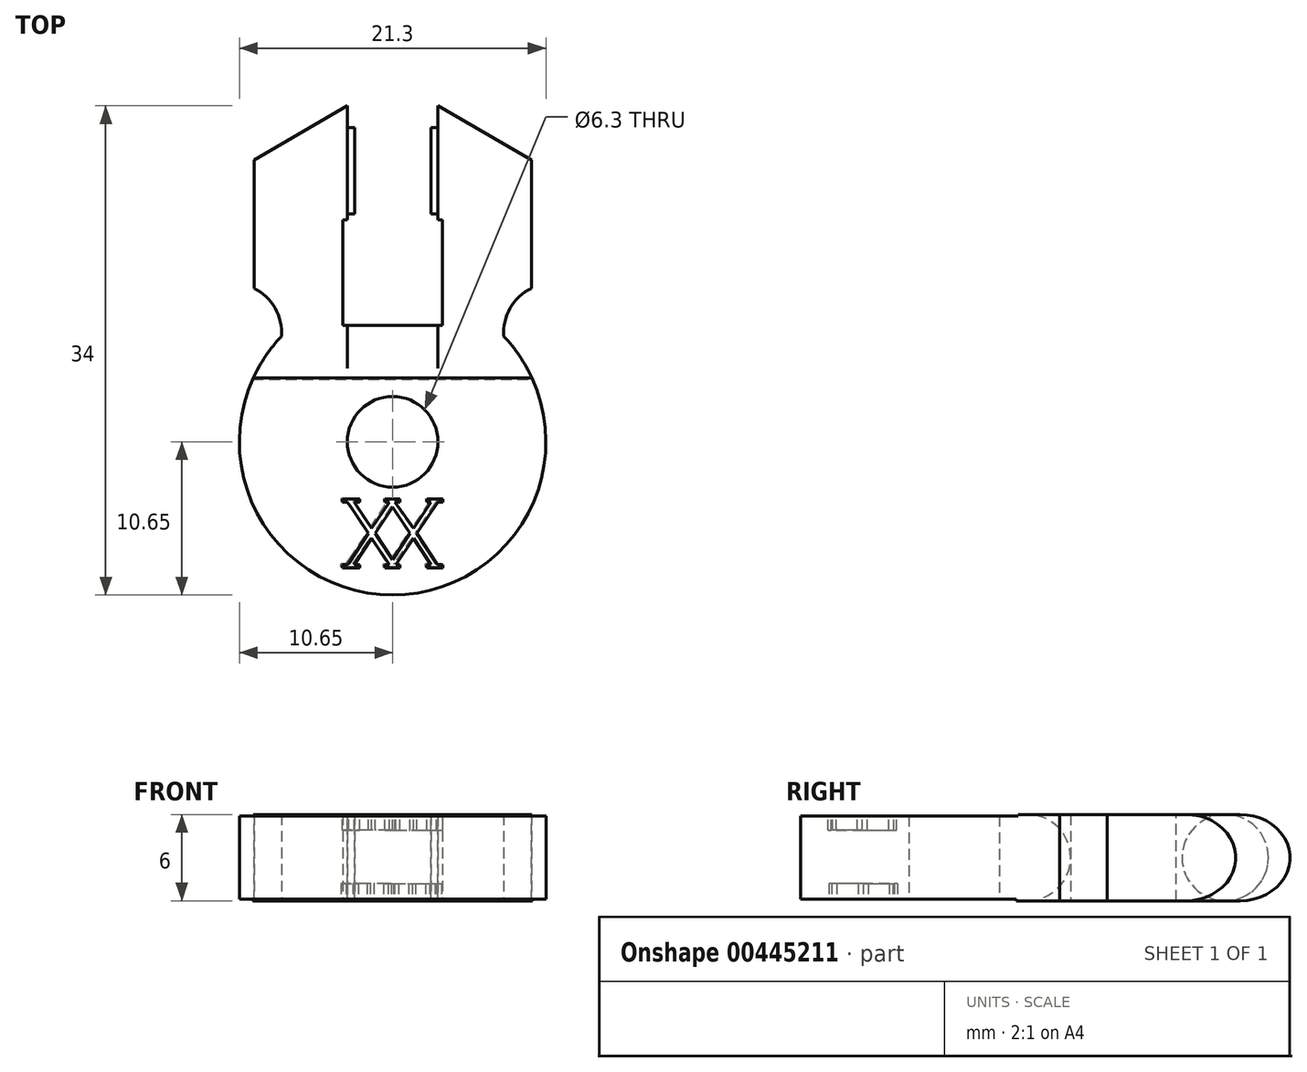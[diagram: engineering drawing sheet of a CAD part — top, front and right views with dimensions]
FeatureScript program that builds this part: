
annotation { "Feature Type Name" : "Feature", "Feature Type Description" : "" }
export const myFeature = defineFeature(function(context is Context, id is Id, definition is map)
    precondition{}
    {
        {
            var Q0;
            Q0=qCreatedBy(makeId("Top.planeOp"),FACE);
            var sketch = newSketch(context, id + "F0", { "sketchPlane" : qUnion([Q0])});
            skArc(sketch, "E0", {"start": v(-3.15, 10.17) * mm, "mid": v(0, -10.65) * mm, "end": v(3.15, 10.17) * mm});
            skCircle(sketch, "E1", {"center": v(0, 0) * mm, "radius": 3.15 * mm});
            skPoint(sketch, "E2", {"position": v(0, 8.1) * mm});
            skLineSegment(sketch, "E3", {"start": v(0, 8.1) * mm, "end": v(3.15, 8.1) * mm});
            skLineSegment(sketch, "E4", {"start": v(0, 8.1) * mm, "end": v(-3.15, 8.1) * mm});
            skLineSegment(sketch, "E5", {"start": v(0, 0) * mm, "end": v(0, 8.1) * mm});
            skLineSegment(sketch, "E6", {"start": v(-3.15, 8.1) * mm, "end": v(-3.15, 23.35) * mm});
            skLineSegment(sketch, "E7", {"start": v(-9.64, 19.59) * mm, "end": v(-9.64, 10.66) * mm});
            skLineSegment(sketch, "E8", {"start": v(-9.64, 19.59) * mm, "end": v(-3.15, 23.35) * mm});
            skArc(sketch, "E9", {"start": v(-7.72, 7.33) * mm, "mid": v(-8.17, 9.3) * mm, "end": v(-9.64, 10.66) * mm});
            skPoint(sketch, "E10.orphan", {"position": v(-9.64, 4.53) * mm});
            skLineSegment(sketch, "E11.MirrorCS", {"start": v(3.15, 8.1) * mm, "end": v(3.15, 23.35) * mm});
            skLineSegment(sketch, "E12.MirrorCS", {"start": v(9.64, 19.59) * mm, "end": v(3.15, 23.35) * mm});
            skLineSegment(sketch, "E13.MirrorCS", {"start": v(9.64, 19.59) * mm, "end": v(9.64, 10.66) * mm});
            skArc(sketch, "E14.MirrorCS", {"start": v(7.72, 7.33) * mm, "mid": v(8.17, 9.3) * mm, "end": v(9.64, 10.66) * mm});
            skSolve(sketch);
        }
        {
            var Q0;
            Q0 = qSketchRegion(id + "F0", true);
            extrude(context, id + "F1", {"entities" : qUnion([Q0]), "depth" : 6 * mm});
        }
        {
            var Q0;
            Q0=makeQuery(id+"F1.opExtrude","SWEPT_FACE",FACE,{"disambiguationData":[OSD([sQuery(id+"F0.wireOp",EDGE,"E6")])]});
            var sketch = newSketch(context, id + "F2", { "sketchPlane" : qUnion([Q0])});
            skLineSegment(sketch, "E15", {"start": v(23.35, 6) * mm, "end": v(23.35, 0) * mm});
            skPoint(sketch, "E16", {"position": v(23.35, 3) * mm});
            skCircle(sketch, "E17", {"center": v(18.85, 3) * mm, "radius": 3 * mm});
            skSolve(sketch);
        }
        {
            var Q0;
            Q0 = qSketchRegion(id + "F2", true);
            extrude(context, id + "F3", {"entities" : qUnion([Q0]), "operationType" : NewBodyOperationType.ADD, "depth" : 0.5 * mm});
        }
        {
            var Q0;
            Q0=makeQuery(id+"F1.opExtrude","SWEPT_FACE",FACE,{"disambiguationData":[OSD([sQuery(id+"F0.wireOp",EDGE,"E11.MirrorCS")])]});
            var sketch = newSketch(context, id + "F4", { "sketchPlane" : qUnion([Q0])});
            skPoint(sketch, "E18", {"position": v(-23.35, 3) * mm});
            skCircle(sketch, "E19", {"center": v(-18.85, 3) * mm, "radius": 3 * mm});
            skSolve(sketch);
        }
        {
            var Q0;
            Q0 = qSketchRegion(id + "F4", true);
            extrude(context, id + "F5", {"entities" : qUnion([Q0]), "operationType" : NewBodyOperationType.ADD, "depth" : 0.5 * mm});
        }
        {
            var Q0;
            Q0=makeQuery(id+"F1.opExtrude","CAP_EDGE",EDGE,{"disambiguationData":[OSD([sQuery(id+"F0.wireOp",EDGE,"E8")])],"isStart":true});
            var Q1;
            Q1=makeQuery(id+"F1.opExtrude","CAP_EDGE",EDGE,{"disambiguationData":[OSD([sQuery(id+"F0.wireOp",EDGE,"E8")])],"isStart":false});
            fillet(context, id + "F6", {"entities" : qUnion([Q0, Q1]), "radius" : 3 * mm, "tangentPropagation" : true, "allowEdgeOverflow" : false});
        }
        {
            var Q0;
            Q0=makeQuery(id+"F1.opExtrude","CAP_EDGE",EDGE,{"disambiguationData":[OSD([sQuery(id+"F0.wireOp",EDGE,"E12.MirrorCS")])],"isStart":true});
            var Q1;
            Q1=makeQuery(id+"F1.opExtrude","CAP_EDGE",EDGE,{"disambiguationData":[OSD([sQuery(id+"F0.wireOp",EDGE,"E12.MirrorCS")])],"isStart":false});
            fillet(context, id + "F7", {"entities" : qUnion([Q0, Q1]), "radius" : 3 * mm, "tangentPropagation" : true, "allowEdgeOverflow" : false});
        }
        {
            var Q0;
            Q0=makeQuery(id+"F1.opExtrude","CAP_FACE",FACE,{"disambiguationData":[OSD([sQuery(id+"F0.wireOp",EDGE,"E0"),sQuery(id+"F0.wireOp",EDGE,"E1"),sQuery(id+"F0.wireOp",EDGE,"E3"),sQuery(id+"F0.wireOp",EDGE,"E4"),sQuery(id+"F0.wireOp",EDGE,"E6"),sQuery(id+"F0.wireOp",EDGE,"E7"),sQuery(id+"F0.wireOp",EDGE,"E8"),sQuery(id+"F0.wireOp",EDGE,"E9"),sQuery(id+"F0.wireOp",EDGE,"E11.MirrorCS"),sQuery(id+"F0.wireOp",EDGE,"E12.MirrorCS"),sQuery(id+"F0.wireOp",EDGE,"E13.MirrorCS"),sQuery(id+"F0.wireOp",EDGE,"E14.MirrorCS")])],"isStart":false});
            var sketch = newSketch(context, id + "F8", { "sketchPlane" : qUnion([Q0])});
            skLineSegment(sketch, "E20.0", {"start": v(-0.23, -4.2) * mm, "end": v(-1.45, -6.02) * mm});
            skLineSegment(sketch, "E21.MirrorCS", {"start": v(0, -4.54) * mm, "end": v(-1.22, -6.37) * mm});
            skLineSegment(sketch, "E22.0", {"start": v(0, -8.2) * mm, "end": v(-1.22, -6.37) * mm});
            skLineSegment(sketch, "E23.MirrorCS", {"start": v(-0.23, -8.54) * mm, "end": v(-1.45, -6.72) * mm});
            skLineSegment(sketch, "E24.trimOffspring", {"start": v(-1.45, -6.02) * mm, "end": v(-2.67, -4.2) * mm});
            skLineSegment(sketch, "E25.trimOffspring", {"start": v(-1.45, -6.72) * mm, "end": v(-2.67, -8.54) * mm});
            skLineSegment(sketch, "E26.trimOffspring", {"start": v(-1.68, -6.37) * mm, "end": v(-2.9, -4.54) * mm});
            skLineSegment(sketch, "E27.trimOffspring", {"start": v(-1.68, -6.37) * mm, "end": v(-3.06, -8.44) * mm});
            skLineSegment(sketch, "E28.MirrorCS", {"start": v(0, -4.54) * mm, "end": v(1.22, -6.37) * mm});
            skLineSegment(sketch, "E29.MirrorCS", {"start": v(1.45, -6.02) * mm, "end": v(2.67, -4.2) * mm});
            skLineSegment(sketch, "E30.MirrorCS", {"start": v(1.68, -6.37) * mm, "end": v(2.9, -4.54) * mm});
            skLineSegment(sketch, "E31.MirrorCS", {"start": v(1.68, -6.37) * mm, "end": v(3.06, -8.44) * mm});
            skLineSegment(sketch, "E32.MirrorCS", {"start": v(1.45, -6.72) * mm, "end": v(2.67, -8.54) * mm});
            skLineSegment(sketch, "E33.MirrorCS", {"start": v(0.23, -8.54) * mm, "end": v(1.45, -6.72) * mm});
            skLineSegment(sketch, "E34.MirrorCS", {"start": v(0, -8.2) * mm, "end": v(1.22, -6.37) * mm});
            skLineSegment(sketch, "E35", {"start": v(0.16, -4.2) * mm, "end": v(0.5, -4.2) * mm});
            skLineSegment(sketch, "E36", {"start": v(-0.23, -4.2) * mm, "end": v(-0.54, -4.2) * mm});
            skLineSegment(sketch, "E37", {"start": v(-2.9, -4.54) * mm, "end": v(-3.13, -4.2) * mm});
            skLineSegment(sketch, "E38", {"start": v(2.9, -4.54) * mm, "end": v(3.13, -4.2) * mm});
            skLineSegment(sketch, "E39", {"start": v(3.06, -8.44) * mm, "end": v(3.14, -8.54) * mm});
            skLineSegment(sketch, "E40", {"start": v(-3.06, -8.44) * mm, "end": v(-3.14, -8.54) * mm});
            skLineSegment(sketch, "E41", {"start": v(-3.5, -4.2) * mm, "end": v(-3.13, -4.2) * mm});
            skLineSegment(sketch, "E42", {"start": v(-0.54, -4.2) * mm, "end": v(-0.23, -4.2) * mm});
            skLineSegment(sketch, "E43", {"start": v(2.38, -4.2) * mm, "end": v(2.67, -4.2) * mm});
            skLineSegment(sketch, "E44", {"start": v(-3.5, -4.2) * mm, "end": v(-3.5, -3.98) * mm});
            skLineSegment(sketch, "E45", {"start": v(-3.5, -3.98) * mm, "end": v(-2.3, -3.98) * mm});
            skLineSegment(sketch, "E46", {"start": v(3.5, -3.98) * mm, "end": v(3.5, -4.2) * mm});
            skLineSegment(sketch, "E47", {"start": v(-2.3, -4.2) * mm, "end": v(-2.3, -3.98) * mm});
            skLineSegment(sketch, "E48", {"start": v(-0.54, -4.2) * mm, "end": v(-0.54, -3.98) * mm});
            skLineSegment(sketch, "E49", {"start": v(0.5, -4.2) * mm, "end": v(0.5, -3.98) * mm});
            skLineSegment(sketch, "E50.trimOffspring", {"start": v(-0.54, -3.98) * mm, "end": v(0.5, -3.98) * mm});
            skLineSegment(sketch, "E51.trimOffspring", {"start": v(-2.3, -4.2) * mm, "end": v(-2.67, -4.2) * mm});
            skLineSegment(sketch, "E52.trimOffspring", {"start": v(-2.67, -4.2) * mm, "end": v(-2.3, -4.2) * mm});
            skLineSegment(sketch, "E53.trimOffspring", {"start": v(-3.13, -4.2) * mm, "end": v(-3.5, -4.2) * mm});
            skLineSegment(sketch, "E54", {"start": v(2.38, -4.2) * mm, "end": v(2.38, -3.98) * mm});
            skLineSegment(sketch, "E55.trimOffspring", {"start": v(2.38, -3.98) * mm, "end": v(3.5, -3.98) * mm});
            skLineSegment(sketch, "E56.trimOffspring", {"start": v(3.13, -4.2) * mm, "end": v(3.36, -4.2) * mm});
            skLineSegment(sketch, "E57.trimOffspring", {"start": v(3.13, -4.2) * mm, "end": v(3.5, -4.2) * mm});
            skLineSegment(sketch, "E58.trimOffspring", {"start": v(3.13, -8.54) * mm, "end": v(3.14, -8.54) * mm});
            skLineSegment(sketch, "E59.MirrorCS", {"start": v(-0.54, -8.75) * mm, "end": v(0.5, -8.75) * mm});
            skLineSegment(sketch, "E60.MirrorCS", {"start": v(-0.54, -8.54) * mm, "end": v(-0.54, -8.75) * mm});
            skLineSegment(sketch, "E61.MirrorCS", {"start": v(-0.23, -8.54) * mm, "end": v(-0.54, -8.54) * mm});
            skLineSegment(sketch, "E62.MirrorCS", {"start": v(0.23, -8.54) * mm, "end": v(0.5, -8.54) * mm});
            skLineSegment(sketch, "E63.MirrorCS", {"start": v(0.5, -8.54) * mm, "end": v(0.5, -8.75) * mm});
            skLineSegment(sketch, "E64.MirrorCS", {"start": v(-3.13, -8.54) * mm, "end": v(-3.5, -8.54) * mm});
            skLineSegment(sketch, "E65.MirrorCS", {"start": v(-3.5, -8.54) * mm, "end": v(-3.5, -8.75) * mm});
            skLineSegment(sketch, "E66.MirrorCS", {"start": v(-3.5, -8.75) * mm, "end": v(-2.3, -8.75) * mm});
            skLineSegment(sketch, "E67.MirrorCS", {"start": v(-2.3, -8.54) * mm, "end": v(-2.3, -8.75) * mm});
            skLineSegment(sketch, "E68.MirrorCS", {"start": v(-2.67, -8.54) * mm, "end": v(-2.3, -8.54) * mm});
            skLineSegment(sketch, "E69.MirrorCS", {"start": v(2.38, -8.75) * mm, "end": v(3.5, -8.75) * mm});
            skLineSegment(sketch, "E70.MirrorCS", {"start": v(3.5, -8.75) * mm, "end": v(3.5, -8.54) * mm});
            skLineSegment(sketch, "E71.MirrorCS", {"start": v(3.13, -8.54) * mm, "end": v(3.5, -8.54) * mm});
            skLineSegment(sketch, "E72.MirrorCS", {"start": v(2.38, -8.54) * mm, "end": v(2.67, -8.54) * mm});
            skLineSegment(sketch, "E73.MirrorCS", {"start": v(2.38, -8.54) * mm, "end": v(2.38, -8.75) * mm});
            skLineSegment(sketch, "E74", {"start": v(0.16, -4.2) * mm, "end": v(1.45, -6.02) * mm});
            skSolve(sketch);
        }
        {
            var Q0;
            Q0 = qSketchRegion(id + "F8", true);
            extrude(context, id + "F9", {"entities" : qUnion([Q0]), "operationType" : NewBodyOperationType.REMOVE, "oppositeDirection" : true, "depth" : 1.1 * mm});
        }
        {
            var Q0;
            Q0=makeQuery(id+"F1.opExtrude","CAP_FACE",FACE,{"disambiguationData":[OSD([sQuery(id+"F0.wireOp",EDGE,"E0"),sQuery(id+"F0.wireOp",EDGE,"E1"),sQuery(id+"F0.wireOp",EDGE,"E3"),sQuery(id+"F0.wireOp",EDGE,"E4"),sQuery(id+"F0.wireOp",EDGE,"E6"),sQuery(id+"F0.wireOp",EDGE,"E7"),sQuery(id+"F0.wireOp",EDGE,"E8"),sQuery(id+"F0.wireOp",EDGE,"E9"),sQuery(id+"F0.wireOp",EDGE,"E11.MirrorCS"),sQuery(id+"F0.wireOp",EDGE,"E12.MirrorCS"),sQuery(id+"F0.wireOp",EDGE,"E13.MirrorCS"),sQuery(id+"F0.wireOp",EDGE,"E14.MirrorCS")])],"isStart":true});
            var sketch = newSketch(context, id + "F10", { "sketchPlane" : qUnion([Q0])});
            skLineSegment(sketch, "E75.0", {"start": v(-0.33, 8.5) * mm, "end": v(-1.55, 6.67) * mm});
            skLineSegment(sketch, "E76.MirrorCS", {"start": v(-0.1, 8.14) * mm, "end": v(-1.32, 6.32) * mm});
            skLineSegment(sketch, "E77.0", {"start": v(-0.1, 4.5) * mm, "end": v(-1.32, 6.32) * mm});
            skLineSegment(sketch, "E78.MirrorCS", {"start": v(-0.33, 4.14) * mm, "end": v(-1.55, 5.97) * mm});
            skLineSegment(sketch, "E79.trimOffspring", {"start": v(-1.55, 6.67) * mm, "end": v(-2.77, 8.5) * mm});
            skLineSegment(sketch, "E80.trimOffspring", {"start": v(-1.55, 5.97) * mm, "end": v(-2.77, 4.14) * mm});
            skLineSegment(sketch, "E81.trimOffspring", {"start": v(-1.78, 6.32) * mm, "end": v(-3, 8.14) * mm});
            skLineSegment(sketch, "E82.trimOffspring", {"start": v(-1.78, 6.32) * mm, "end": v(-3.16, 4.25) * mm});
            skLineSegment(sketch, "E83.MirrorCS", {"start": v(-0.1, 8.14) * mm, "end": v(1.12, 6.32) * mm});
            skLineSegment(sketch, "E84.MirrorCS", {"start": v(1.35, 6.67) * mm, "end": v(2.57, 8.5) * mm});
            skLineSegment(sketch, "E85.MirrorCS", {"start": v(1.58, 6.32) * mm, "end": v(2.8, 8.14) * mm});
            skLineSegment(sketch, "E86.MirrorCS", {"start": v(1.58, 6.32) * mm, "end": v(2.96, 4.25) * mm});
            skLineSegment(sketch, "E87.MirrorCS", {"start": v(1.35, 5.97) * mm, "end": v(2.57, 4.14) * mm});
            skLineSegment(sketch, "E88.MirrorCS", {"start": v(0.13, 4.14) * mm, "end": v(1.35, 5.97) * mm});
            skLineSegment(sketch, "E89.MirrorCS", {"start": v(-0.1, 4.5) * mm, "end": v(1.12, 6.32) * mm});
            skLineSegment(sketch, "E90", {"start": v(0.06, 8.5) * mm, "end": v(0.4, 8.5) * mm});
            skLineSegment(sketch, "E91", {"start": v(-0.33, 8.5) * mm, "end": v(-0.64, 8.5) * mm});
            skLineSegment(sketch, "E92", {"start": v(-3, 8.14) * mm, "end": v(-3.23, 8.5) * mm});
            skLineSegment(sketch, "E93", {"start": v(2.8, 8.14) * mm, "end": v(3.03, 8.5) * mm});
            skLineSegment(sketch, "E94", {"start": v(2.96, 4.25) * mm, "end": v(3.04, 4.14) * mm});
            skLineSegment(sketch, "E95", {"start": v(-3.16, 4.25) * mm, "end": v(-3.24, 4.14) * mm});
            skLineSegment(sketch, "E96", {"start": v(-3.6, 8.5) * mm, "end": v(-3.23, 8.5) * mm});
            skLineSegment(sketch, "E97", {"start": v(-0.64, 8.5) * mm, "end": v(-0.33, 8.5) * mm});
            skLineSegment(sketch, "E98", {"start": v(2.28, 8.5) * mm, "end": v(2.57, 8.5) * mm});
            skLineSegment(sketch, "E99", {"start": v(-3.6, 8.5) * mm, "end": v(-3.6, 8.7) * mm});
            skLineSegment(sketch, "E100", {"start": v(-3.6, 8.7) * mm, "end": v(-2.4, 8.7) * mm});
            skLineSegment(sketch, "E101", {"start": v(3.4, 8.7) * mm, "end": v(3.4, 8.5) * mm});
            skLineSegment(sketch, "E102", {"start": v(-2.4, 8.5) * mm, "end": v(-2.4, 8.7) * mm});
            skLineSegment(sketch, "E103", {"start": v(-0.64, 8.5) * mm, "end": v(-0.64, 8.7) * mm});
            skLineSegment(sketch, "E104", {"start": v(0.4, 8.5) * mm, "end": v(0.4, 8.7) * mm});
            skLineSegment(sketch, "E105.trimOffspring", {"start": v(-0.64, 8.7) * mm, "end": v(0.4, 8.7) * mm});
            skLineSegment(sketch, "E106.trimOffspring", {"start": v(-2.4, 8.5) * mm, "end": v(-2.77, 8.5) * mm});
            skLineSegment(sketch, "E107.trimOffspring", {"start": v(-2.77, 8.5) * mm, "end": v(-2.4, 8.5) * mm});
            skLineSegment(sketch, "E108.trimOffspring", {"start": v(-3.23, 8.5) * mm, "end": v(-3.6, 8.5) * mm});
            skLineSegment(sketch, "E109", {"start": v(2.28, 8.5) * mm, "end": v(2.28, 8.7) * mm});
            skLineSegment(sketch, "E110.trimOffspring", {"start": v(2.28, 8.7) * mm, "end": v(3.4, 8.7) * mm});
            skLineSegment(sketch, "E111.trimOffspring", {"start": v(3.03, 8.5) * mm, "end": v(3.26, 8.5) * mm});
            skLineSegment(sketch, "E112.trimOffspring", {"start": v(3.03, 8.5) * mm, "end": v(3.4, 8.5) * mm});
            skLineSegment(sketch, "E113.trimOffspring", {"start": v(3.03, 4.14) * mm, "end": v(3.04, 4.14) * mm});
            skLineSegment(sketch, "E114.MirrorCS", {"start": v(-0.64, 3.93) * mm, "end": v(0.4, 3.93) * mm});
            skLineSegment(sketch, "E115.MirrorCS", {"start": v(-0.64, 4.14) * mm, "end": v(-0.64, 3.93) * mm});
            skLineSegment(sketch, "E116.MirrorCS", {"start": v(-0.33, 4.14) * mm, "end": v(-0.64, 4.14) * mm});
            skLineSegment(sketch, "E117.MirrorCS", {"start": v(0.13, 4.14) * mm, "end": v(0.4, 4.14) * mm});
            skLineSegment(sketch, "E118.MirrorCS", {"start": v(0.4, 4.14) * mm, "end": v(0.4, 3.93) * mm});
            skLineSegment(sketch, "E119.MirrorCS", {"start": v(-3.23, 4.14) * mm, "end": v(-3.6, 4.14) * mm});
            skLineSegment(sketch, "E120.MirrorCS", {"start": v(-3.6, 4.14) * mm, "end": v(-3.6, 3.93) * mm});
            skLineSegment(sketch, "E121.MirrorCS", {"start": v(-3.6, 3.93) * mm, "end": v(-2.4, 3.93) * mm});
            skLineSegment(sketch, "E122.MirrorCS", {"start": v(-2.4, 4.14) * mm, "end": v(-2.4, 3.93) * mm});
            skLineSegment(sketch, "E123.MirrorCS", {"start": v(-2.77, 4.14) * mm, "end": v(-2.4, 4.14) * mm});
            skLineSegment(sketch, "E124.MirrorCS", {"start": v(2.28, 3.93) * mm, "end": v(3.4, 3.93) * mm});
            skLineSegment(sketch, "E125.MirrorCS", {"start": v(3.4, 3.93) * mm, "end": v(3.4, 4.14) * mm});
            skLineSegment(sketch, "E126.MirrorCS", {"start": v(3.03, 4.14) * mm, "end": v(3.4, 4.14) * mm});
            skLineSegment(sketch, "E127.MirrorCS", {"start": v(2.28, 4.14) * mm, "end": v(2.57, 4.14) * mm});
            skLineSegment(sketch, "E128.MirrorCS", {"start": v(2.28, 4.14) * mm, "end": v(2.28, 3.93) * mm});
            skLineSegment(sketch, "E129", {"start": v(0.06, 8.5) * mm, "end": v(1.35, 6.67) * mm});
            skSolve(sketch);
        }
        {
            var Q0;
            Q0 = qSketchRegion(id + "F10", true);
            extrude(context, id + "F11", {"entities" : qUnion([Q0]), "operationType" : NewBodyOperationType.REMOVE, "oppositeDirection" : true, "depth" : 1.2 * mm});
        }
        {
            var Q0;
            Q0=makeQuery(id+"F1.opExtrude","CAP_EDGE",EDGE,{"disambiguationData":[OSD([sQuery(id+"F0.wireOp",EDGE,"E3"),sQuery(id+"F0.wireOp",EDGE,"E4")])],"isStart":true});
            var Q1;
            Q1=makeQuery(id+"F1.opExtrude","CAP_EDGE",EDGE,{"disambiguationData":[OSD([sQuery(id+"F0.wireOp",EDGE,"E3"),sQuery(id+"F0.wireOp",EDGE,"E4")])],"isStart":false});
            fillet(context, id + "F12", {"entities" : qUnion([Q0, Q1]), "radius" : 3 * mm, "tangentPropagation" : true, "allowEdgeOverflow" : false});
        }
        {
            var Q0;
            Q0=qCreatedBy(makeId("Top.planeOp"),FACE);
            var sketch = newSketch(context, id + "F13", { "sketchPlane" : qUnion([Q0])});
            skLineSegment(sketch, "E130", {"start": v(3.15, 8.1) * mm, "end": v(3.12, 8.1) * mm});
            skLineSegment(sketch, "E131", {"start": v(-3.12, 8.1) * mm, "end": v(-3.45, 8.1) * mm});
            skLineSegment(sketch, "E132", {"start": v(-3.45, 8.1) * mm, "end": v(-3.45, 15.43) * mm});
            skLineSegment(sketch, "E133", {"start": v(-3.45, 15.43) * mm, "end": v(-3.13, 15.43) * mm});
            skLineSegment(sketch, "E134.MirrorCS", {"start": v(3.45, 8.1) * mm, "end": v(3.45, 15.43) * mm});
            skLineSegment(sketch, "E135.MirrorCS", {"start": v(3.12, 8.1) * mm, "end": v(3.45, 8.1) * mm});
            skLineSegment(sketch, "E136.MirrorCS", {"start": v(3.45, 15.43) * mm, "end": v(3.13, 15.43) * mm});
            skLineSegment(sketch, "E137", {"start": v(-3.12, 8.1) * mm, "end": v(-3.13, 15.43) * mm});
            skLineSegment(sketch, "E138", {"start": v(3.15, 8.1) * mm, "end": v(3.13, 15.43) * mm});
            skSolve(sketch);
        }
        {
            var Q0;
            Q0 = qSketchRegion(id + "F13", true);
            extrude(context, id + "F14", {"entities" : qUnion([Q0]), "operationType" : NewBodyOperationType.REMOVE, "depth" : 13.4 * mm});
        }
        {
            var Q0;
            {var subQ0=sQuery(id+"F0.wireOp",EDGE,"E4");var subQ1=sQuery(id+"F0.wireOp",EDGE,"E3");var subQ2=sQuery(id+"F0.wireOp",EDGE,"E11.MirrorCS");var subQ3=sQuery(id+"F0.wireOp",EDGE,"E9");var subQ4=sQuery(id+"F0.wireOp",EDGE,"E7");var subQ5=sQuery(id+"F0.wireOp",EDGE,"E0");var subQ6=sQuery(id+"F0.wireOp",EDGE,"E1");var subQ7=sQuery(id+"F0.wireOp",EDGE,"E14.MirrorCS");var subQ8=sQuery(id+"F0.wireOp",EDGE,"E8");var subQ9=sQuery(id+"F0.wireOp",EDGE,"E12.MirrorCS");var subQ10=sQuery(id+"F0.wireOp",EDGE,"E13.MirrorCS");var subQ11=sQuery(id+"F0.wireOp",EDGE,"E6");Q0=makeQuery(id+"F11.boolean.opBoolean","SPLIT",FACE,{"disambiguationData":[TD([makeQuery(id+"F1.opExtrude","SWEPT_FACE",FACE,{"disambiguationData":[OSD([subQ5])]})])],"derivedFrom":makeQuery(id+"F1.opExtrude","CAP_FACE",FACE,{"disambiguationData":[OSD([subQ5,subQ6,subQ1,subQ0,subQ11,subQ4,subQ8,subQ3,subQ2,subQ9,subQ10,subQ7])],"isStart":true})});}
            var sketch = newSketch(context, id + "F15", { "sketchPlane" : qUnion([Q0])});
            skArc(sketch, "E139", {"start": v(9.76, -4.34) * mm, "mid": v(0, 10.68) * mm, "end": v(-9.76, -4.34) * mm});
            skLineSegment(sketch, "E140", {"start": v(-9.73, -4.34) * mm, "end": v(9.73, -4.34) * mm});
            skLineSegment(sketch, "E141", {"start": v(-9.76, -4.34) * mm, "end": v(-9.73, -4.34) * mm});
            skLineSegment(sketch, "E142.trimOffspring", {"start": v(9.73, -4.34) * mm, "end": v(9.76, -4.34) * mm});
            skSolve(sketch);
        }
        {
            var Q0;
            Q0 = qSketchRegion(id + "F15", true);
            extrude(context, id + "F16", {"entities" : qUnion([Q0]), "operationType" : NewBodyOperationType.REMOVE, "oppositeDirection" : true, "depth" : 0.1 * mm});
        }
        {
            var Q0;
            {var subQ0=sQuery(id+"F0.wireOp",EDGE,"E13.MirrorCS");var subQ1=sQuery(id+"F0.wireOp",EDGE,"E9");var subQ2=sQuery(id+"F0.wireOp",EDGE,"E11.MirrorCS");var subQ3=sQuery(id+"F0.wireOp",EDGE,"E4");var subQ4=sQuery(id+"F0.wireOp",EDGE,"E3");var subQ5=sQuery(id+"F0.wireOp",EDGE,"E0");var subQ6=sQuery(id+"F0.wireOp",EDGE,"E7");var subQ7=sQuery(id+"F0.wireOp",EDGE,"E6");var subQ8=sQuery(id+"F0.wireOp",EDGE,"E1");var subQ9=sQuery(id+"F0.wireOp",EDGE,"E8");var subQ10=sQuery(id+"F0.wireOp",EDGE,"E14.MirrorCS");var subQ11=sQuery(id+"F0.wireOp",EDGE,"E12.MirrorCS");Q0=makeQuery(id+"F9.boolean.opBoolean","SPLIT",FACE,{"disambiguationData":[TD([makeQuery(id+"F1.opExtrude","SWEPT_FACE",FACE,{"disambiguationData":[OSD([subQ5])]})])],"derivedFrom":makeQuery(id+"F1.opExtrude","CAP_FACE",FACE,{"disambiguationData":[OSD([subQ5,subQ8,subQ4,subQ3,subQ7,subQ6,subQ9,subQ1,subQ2,subQ11,subQ0,subQ10])],"isStart":false})});}
            var sketch = newSketch(context, id + "F17", { "sketchPlane" : qUnion([Q0])});
            skArc(sketch, "E143", {"start": v(-9.68, 4.44) * mm, "mid": v(0, -10.65) * mm, "end": v(9.68, 4.44) * mm});
            skLineSegment(sketch, "E144", {"start": v(9.65, 4.44) * mm, "end": v(-9.8, 4.44) * mm});
            skLineSegment(sketch, "E145", {"start": v(9.68, 4.44) * mm, "end": v(9.65, 4.44) * mm});
            skLineSegment(sketch, "E146.trimOffspring", {"start": v(-9.68, 4.44) * mm, "end": v(-9.8, 4.44) * mm});
            skSolve(sketch);
        }
        {
            var Q0;
            Q0 = qSketchRegion(id + "F17", true);
            extrude(context, id + "F18", {"entities" : qUnion([Q0]), "operationType" : NewBodyOperationType.REMOVE, "oppositeDirection" : true, "depth" : 0.1 * mm});
        }
    });
